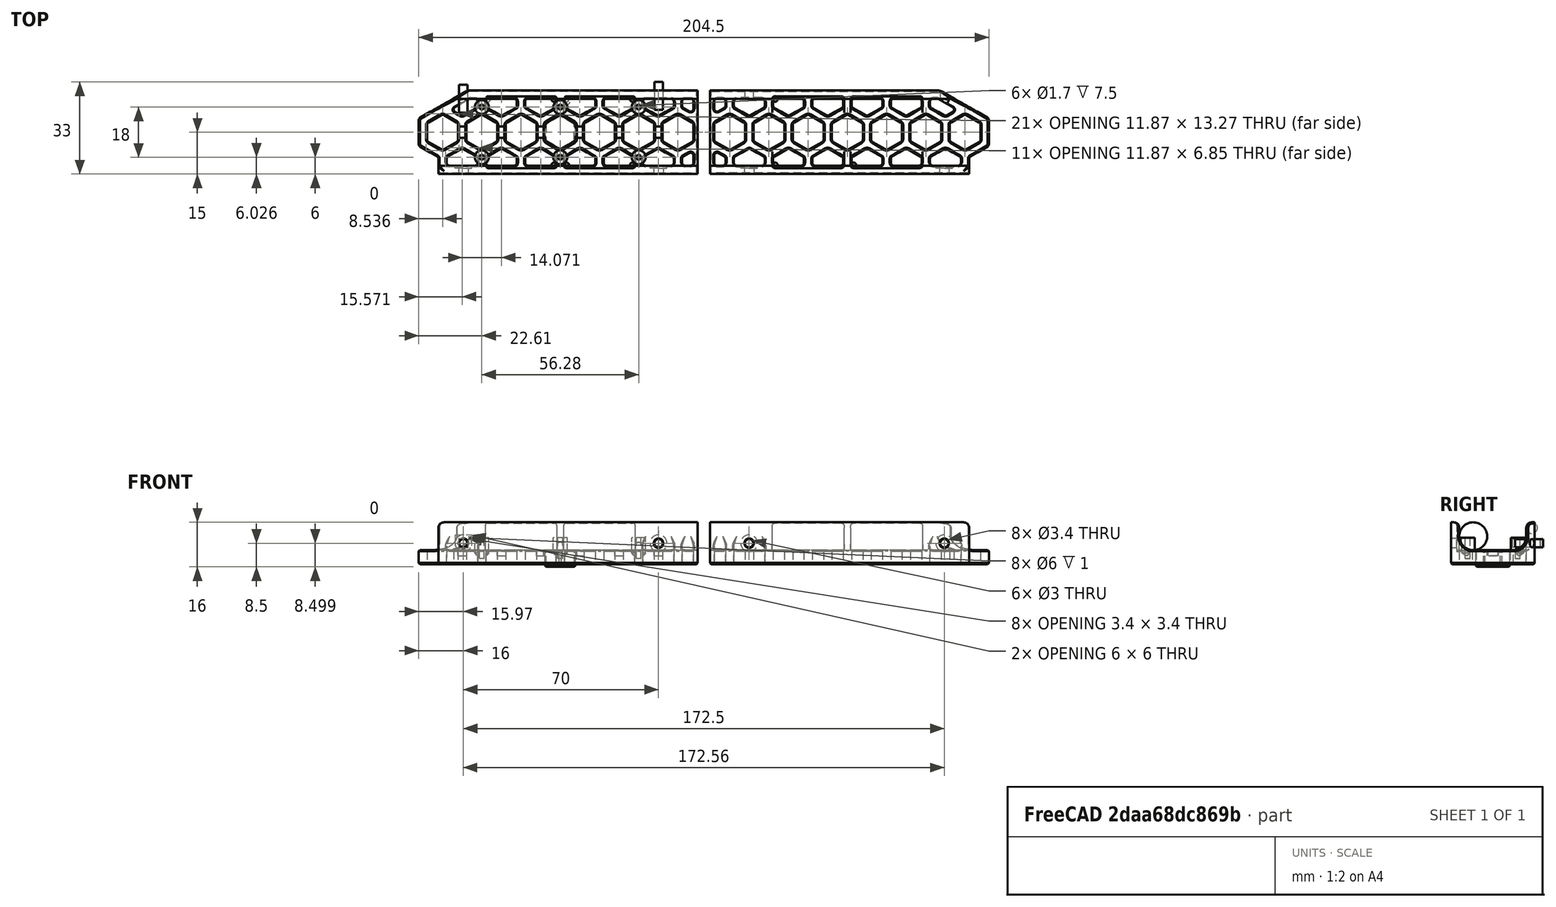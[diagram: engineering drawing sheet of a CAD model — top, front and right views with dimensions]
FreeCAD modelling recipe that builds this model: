
FCSTD DOCUMENT  (FreeCAD 0.18R16146 (Git))
Label: skirt-button
License: All rights reserved
LicenseURL: http://en.wikipedia.org/wiki/All_rights_reserved
objects: Part::Cylinder×14, Part::Feature×9, Part::MultiFuse×6, Part::Cut×4, Part::Chamfer×3, Part::Box×2
note: 38 computed .brp shape members not serialized (recipe doc carries the construction recipe); baked Part::Feature solids carry a one-line shape summary decoded from their .brp

FEATURE [Part::Feature] Part__Feature1066  label="v0 foot_skirt004"
  Placement = pos=(-65.75,20,-0.000778452) rot=(1,0,0;3.14159rad)
  shape: bbox 100 x 30 x 15 mm, 789 faces (baked)
FEATURE [Part::Cylinder] Cylinder002
  Angle = 360
  AttacherType = Attacher::AttachEngine3D
  Height = 8
  Placement = pos=(0,14,0) rot=(0,0,1;0rad)
  Radius = 0.85
FEATURE [Part::Cylinder] Cylinder005
  Angle = 360
  AttacherType = Attacher::AttachEngine3D
  Height = 8
  Placement = pos=(-28.14,14,0) rot=(0,0,1;0rad)
  Radius = 0.85
FEATURE [Part::Cylinder] Cylinder006
  Angle = 360
  AttacherType = Attacher::AttachEngine3D
  Height = 8
  Placement = pos=(28.14,14,0) rot=(0,0,1;0rad)
  Radius = 0.85
FEATURE [Part::Cylinder] Cylinder007
  Angle = 360
  AttacherType = Attacher::AttachEngine3D
  Height = 8
  Placement = pos=(-28.14,-4,0) rot=(0,0,1;0rad)
  Radius = 0.85
FEATURE [Part::Cylinder] Cylinder008
  Angle = 360
  AttacherType = Attacher::AttachEngine3D
  Height = 8
  Placement = pos=(0,-4,0) rot=(0,0,1;0rad)
  Radius = 0.85
FEATURE [Part::Cylinder] Cylinder009
  Angle = 360
  AttacherType = Attacher::AttachEngine3D
  Height = 8
  Placement = pos=(28.14,-4,0) rot=(0,0,1;0rad)
  Radius = 0.85
FEATURE [Part::Cylinder] Cylinder010
  Angle = 360
  AttacherType = Attacher::AttachEngine3D
  Height = 5
  Placement = pos=(28.14,-4,0) rot=(0,0,1;0rad)
  Radius = 2.5
FEATURE [Part::Cylinder] Cylinder011
  Angle = 360
  AttacherType = Attacher::AttachEngine3D
  Height = 5
  Placement = pos=(-28.14,-4,0) rot=(0,0,1;0rad)
  Radius = 2.5
FEATURE [Part::Cylinder] Cylinder012
  Angle = 360
  AttacherType = Attacher::AttachEngine3D
  Height = 5
  Placement = pos=(0,-4,0) rot=(0,0,1;0rad)
  Radius = 2.5
FEATURE [Part::Cylinder] Cylinder013
  Angle = 360
  AttacherType = Attacher::AttachEngine3D
  Height = 5
  Placement = pos=(28.14,14,0) rot=(0,0,1;0rad)
  Radius = 2.5
FEATURE [Part::Cylinder] Cylinder014
  Angle = 360
  AttacherType = Attacher::AttachEngine3D
  Height = 5
  Placement = pos=(-28.14,14,0) rot=(0,0,1;0rad)
  Radius = 2.5
FEATURE [Part::Cylinder] Cylinder015
  Angle = 360
  AttacherType = Attacher::AttachEngine3D
  Height = 5
  Placement = pos=(0,14,0) rot=(0,0,1;0rad)
  Radius = 2.5
FEATURE [Part::MultiFuse] Fusion
  Placement = pos=(0,0,3) rot=(0,0,1;0rad)
  Shapes = -> [Cylinder015,Cylinder014,Cylinder013,Cylinder012,Cylinder011,Cylinder010]
FEATURE [Part::MultiFuse] Fusion002
  Placement = pos=(0,0,2) rot=(0,0,1;0rad)
  Shapes = -> [Cylinder009,Cylinder002,Cylinder007,Cylinder008,Cylinder005,Cylinder006]
FEATURE [Part::Box] Box  label="Cube"
  AttacherType = Attacher::AttachEngine3D
  Height = 10
  Length = 77
  Placement = pos=(-38,3,3) rot=(0,0,1;0rad)
  Width = 4
FEATURE [Part::Cylinder] Cylinder
  Angle = 360
  AttacherType = Attacher::AttachEngine3D
  Height = 10
  Placement = pos=(-34.78,22,7.5) rot=(1,0,0;1.5708rad)
  Radius = 1.5
FEATURE [Part::Cylinder] Cylinder016
  Angle = 360
  AttacherType = Attacher::AttachEngine3D
  Height = 10
  Placement = pos=(35.275,23,7.5) rot=(1,0,0;1.5708rad)
  Radius = 1.5
FEATURE [Part::Feature] Part__Feature1067  label="v0 foot_skirt005"
  Placement = pos=(-65.75,20,-0.000778452) rot=(1,0,0;3.14159rad)
  shape: bbox 100 x 30 x 15 mm, 789 faces (baked)
FEATURE [Part::MultiFuse] Fusion003  label="drill"
  Shapes = -> [Cylinder,Cylinder016]
FEATURE [Part::Feature] Fusion003001  label="drill001"
  shape: bbox 73.06 x 11 x 3 mm, 6 faces, 2 solids (baked)
FEATURE [Part::Feature] Fusion003002  label="drill002"
  shape: bbox 73.06 x 11 x 3 mm, 6 faces, 2 solids (baked)
FEATURE [Part::Feature] Part__Feature1067001  label="v0 foot_skirt006"
  Placement = pos=(-65.75,20,-0.000778452) rot=(1,0,0;3.14159rad)
  shape: bbox 100 x 30 x 15 mm, 789 faces (baked)
FEATURE [Part::Cut] Cut003  label="common-left"
  Base = -> Part__Feature1067001
  Tool = -> Fusion003002
FEATURE [Part::Feature] Part__Mirroring001  label="common-right"
  Placement = pos=(103,0,0) rot=(0,0,1;0rad)
  shape: bbox 100 x 30 x 15 mm, 792 faces (baked)
FEATURE [Part::Feature] Cut003001  label="common-left001"
  shape: bbox 100 x 30 x 15 mm, 792 faces (baked)
FEATURE [Part::Box] Box001  label="Cube001"
  AttacherType = Attacher::AttachEngine3D
  Height = 2
  Length = 12
  Placement = pos=(-6,-1.75,4) rot=(0,0,1;0rad)
  Width = 3.5
FEATURE [Part::Chamfer] Chamfer002
  Base = -> Box001
  Edges = 4 edges r=0.4: [Edge9,Edge10,Edge11,Edge12]
FEATURE [Part::Chamfer] Chamfer
  Base = -> Fusion
  Edges = 6 edges r=1: [Edge3,Edge6,Edge9,Edge12,Edge15,Edge18]
FEATURE [Part::Feature] Fusion003004
  Placement = pos=(0,0,4.5) rot=(0,0,1;0rad)
  shape: bbox 61.28 x 23 x 5 mm, 18 faces, 6 solids (baked)
FEATURE [Part::MultiFuse] Fusion003005
  Shapes = -> [Fusion003004,Chamfer]
FEATURE [Part::MultiFuse] Fusion003006
  Shapes = -> [Part__Feature1066,Fusion003005]
FEATURE [Part::Cut] Cut
  Base = -> Fusion003006
  Tool = -> Fusion002
FEATURE [Part::Cut] Cut003004
  Base = -> Cut
  Tool = -> Box
FEATURE [Part::Cut] Cut003005  label="front-left"
  Base = -> Cut003004
  Tool = -> Fusion003001
FEATURE [Part::Feature] Body001
  shape: bbox 10.83 x 12.5 x 6 mm, 8 faces (baked)
FEATURE [Part::Chamfer] Chamfer003
  Base = -> Body001
  Edges = 12 edges r=0.4: [Edge1,Edge2,Edge3,Edge5,Edge6,Edge8,Edge9,Edge11,Edge12,Edge14,Edge15,Edge17]
FEATURE [Part::MultiFuse] Fusion003007  label="button"
  Placement = pos=(0,5,-1) rot=(0,0,1;0rad)
  Shapes = -> [Chamfer003,Chamfer002]
